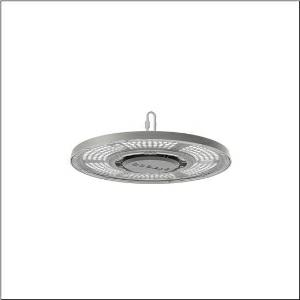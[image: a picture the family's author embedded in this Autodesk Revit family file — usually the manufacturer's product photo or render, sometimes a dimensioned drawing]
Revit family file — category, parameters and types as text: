
# Revit family: highbay_31-s_51hc427a4fmb
name_source: partatom
category: Lighting Fixtures
units: mm (PartAtom-declared; Revit-internal decimal feet)

## family parameters
Cut with Voids When Loaded = No
Host = Face
Light Source = No
Part Type = Normal
Room Calculation Point = No
Round Connector Dimension = Use Diameter
Shared = No

## types (1)
- Highbay 31-S (1 x LED, 14000 lm, 94 W, 4000K)
    Apparent Load = 94 VA
    CIE Flux Codes = 77 99 100 100 100
    Color Rendering = 80
    Color Temperature = 4000K
    Default Elevation = 1800 mm
    Description = Highbay 31-S, LED high bay luminaire, primary light control with lens, of PC, primary optical cover: cover panel, of PC, transparent, light emission: direct distribution, primary light characteristic: rotationally symmetric, installation type: suspended mounting, surface-mounted, LED, rated luminous flux: 14.000lm, luminous efficacy: 150lm/W, light colour: 840, colour temperature: 4000K, control gear: ECG, with cable, 3x 1.0mm², free wire ends, mains connection: 220..240V, AC/DC, 0/50..60Hz, cable length: 1,5m, rated input power: 94W, housing, rotationally symmetric, of diecast aluminium, grey aluminium (RAL 9007), diameter: 339mm, protection rating (complete): IP65, insulation class (complete): insulation class I (protective earthing), certification: CE, ENEC, UKCA, protection symbol: D, impact resistance: IK08, permissible operating ambient temperature: -30..+45°C, standard: EN 60598-2-22, EN 60598, corresponds to IFS (International Featured Standards) requirements for safety and quality in the food industry, packaging unit: 1 piece
    Height = 141 mm
    Lamp = 1 x LED
    Lamp Light Flux = 14000 lm
    Lamp Power = 94 W
    Lamp count = 1
    Length = 339 mm
    Luminous efficacy = 149 lm/W
    Manufacturer = Siteco
    ModVariant = No
    Model = 51HC427A4FMB
    Mounting Place = Ceiling
    Mounting Type = Pendant
    Number of Poles = 1
    OnlyDefault = Yes
    Power Factor = 1
    Product Name = Highbay 31-S
    Product group = LED high bay luminaire
    ProductGroupID = 903
    Protection Class = Protection class I
    Protection Degree = IP 65
    RLX_Detail_Level = 1
    RlxData = <blob elided: 163265 chars, md5=4daeeeab>
    Socket = socket
    Standby Power = 0 W
    System Light Flux = 14000 lm
    System Power = 94 W
    Type Comments = Product without accessories
    Type Image = l_1007237.jpg
    URL = http://relux.com
    VarID = ---
    Voltage = 0 V
    Weight = 0.00 kg
    Width = 0 mm  [stored 0 ft]

note: [stored X ft] marks values corroborated as IEEE doubles in the binary element streams (Revit-internal decimal feet)

## geometry (parser evidence)
native form markers: Blend x4, Sweep x9
no freeform markers — native parametric forms only
